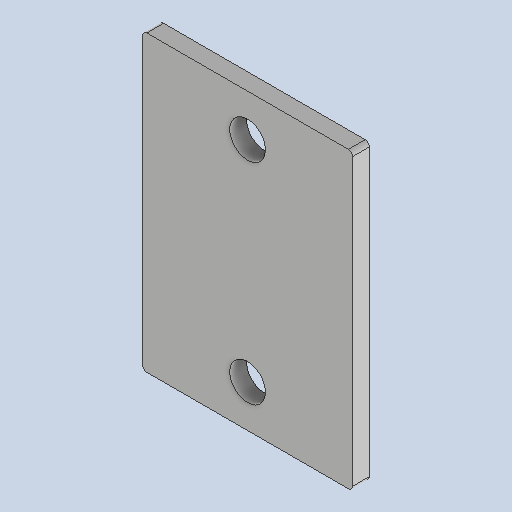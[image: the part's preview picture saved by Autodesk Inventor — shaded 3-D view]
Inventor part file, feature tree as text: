
AUTODESK INVENTOR PART (.ipt)
format: ipt  version: 2025 (Build 290162010, 162A)  size: 114,688 bytes
history: native  units: mm
features: sketch x2, sheet_metal_op x1, hole x1, fillet x1, other x1
ambient origin geometry x8: Origin, YZ Plane, XZ Plane, XY Plane, X Axis, Y Axis, Z Axis, Center Point
bodies: Solid1 (feature_tree)
feature tree (6):
  sheet_metal_op  "Face1"
  hole  "Hole1"  [1 undecoded]
  fillet  "Fillet1"  Radius=8.0mm
  sketch  "Sketch1"  dims[d0=100.0mm d1=140.0mm d2=8.0mm]
  other  "Plate1"
  sketch  "Sketch2"  dims[d3=17.0mm d4=6.0mm d5=4.0mm d6=2.0mm d7=90.0deg d8=8.0mm d9=20.594885mm d16=2.0mm d17=100.0mm]
note: 1 required parameter value undecoded (feature->parameter linkage not recoverable at this tier; creation-order binding heuristic only, values carry confidence <= 0.55)
